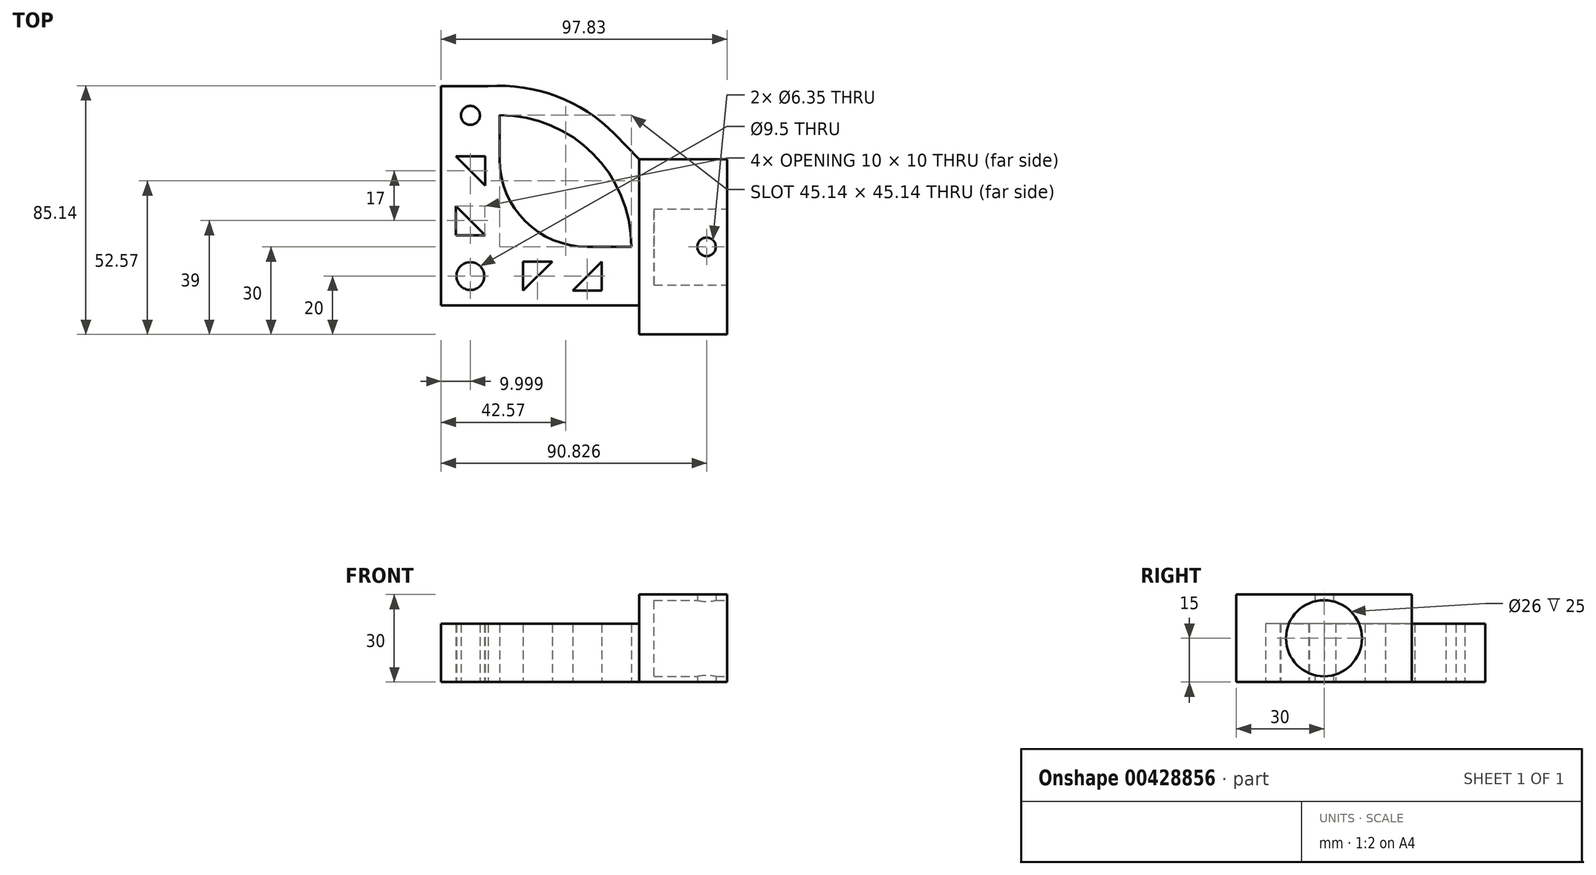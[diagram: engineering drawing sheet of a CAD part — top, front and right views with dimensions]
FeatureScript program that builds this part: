
annotation { "Feature Type Name" : "Feature", "Feature Type Description" : "" }
export const myFeature = defineFeature(function(context is Context, id is Id, definition is map)
    precondition{}
    {
        {
            var Q0;
            Q0=qCreatedBy(makeId("Top.planeOp"),FACE);
            var sketch = newSketch(context, id + "F0", { "sketchPlane" : qUnion([Q0])});
            skLineSegment(sketch, "E0.bottom", {"start": v(-29.45, 49.47) * mm, "end": v(-9.45, 49.47) * mm});
            skLineSegment(sketch, "E0.top", {"start": v(-29.45, -25.53) * mm, "end": v(-9.45, -25.53) * mm});
            skLineSegment(sketch, "E0.left", {"start": v(-29.45, 49.47) * mm, "end": v(-29.45, -25.53) * mm});
            skLineSegment(sketch, "E0.right", {"start": v(-9.45, 49.47) * mm, "end": v(-9.45, 24.47) * mm});
            skLineSegment(sketch, "E1.left", {"start": v(-9.45, -5.53) * mm, "end": v(-9.45, -25.53) * mm});
            skCircle(sketch, "E2", {"center": v(-19.45, -15.53) * mm, "radius": 4.75 * mm});
            skCircle(sketch, "E3", {"center": v(-19.45, 39.47) * mm, "radius": 3.25 * mm});
            skLineSegment(sketch, "E4", {"start": v(15.55, -20.53) * mm, "end": v(25.55, -10.53) * mm});
            skLineSegment(sketch, "E5", {"start": v(25.55, -10.53) * mm, "end": v(25.55, -20.53) * mm});
            skLineSegment(sketch, "E6", {"start": v(25.55, -20.53) * mm, "end": v(15.55, -20.53) * mm});
            skLineSegment(sketch, "E7", {"start": v(8.55, -10.53) * mm, "end": v(-1.45, -20.53) * mm});
            skLineSegment(sketch, "E8", {"start": v(-1.45, -20.53) * mm, "end": v(-1.45, -10.53) * mm});
            skLineSegment(sketch, "E9", {"start": v(-1.45, -10.53) * mm, "end": v(8.55, -10.53) * mm});
            skLineSegment(sketch, "E10", {"start": v(-14.45, 15.47) * mm, "end": v(-24.45, 25.47) * mm});
            skLineSegment(sketch, "E11", {"start": v(-24.45, 25.47) * mm, "end": v(-14.45, 25.47) * mm});
            skLineSegment(sketch, "E12", {"start": v(-14.45, 25.47) * mm, "end": v(-14.45, 15.47) * mm});
            skLineSegment(sketch, "E13", {"start": v(-24.45, 8.47) * mm, "end": v(-14.45, -1.53) * mm});
            skLineSegment(sketch, "E14", {"start": v(-14.45, -1.53) * mm, "end": v(-24.45, -1.53) * mm});
            skLineSegment(sketch, "E15", {"start": v(-24.45, -1.53) * mm, "end": v(-24.45, 8.47) * mm});
            skArc(sketch, "E16.filletArc", {"start": v(-9.45, 24.47) * mm, "mid": v(-0.66, 3.26) * mm, "end": v(20.55, -5.53) * mm});
            skLineSegment(sketch, "E17.bottom", {"start": v(38.38, -35.53) * mm, "end": v(68.38, -35.53) * mm});
            skLineSegment(sketch, "E17.top", {"start": v(38.38, 24.47) * mm, "end": v(68.38, 24.47) * mm});
            skLineSegment(sketch, "E17.right", {"start": v(68.38, -35.53) * mm, "end": v(68.38, 24.47) * mm});
            skLineSegment(sketch, "E18", {"start": v(-9.45, -25.53) * mm, "end": v(38.38, -25.53) * mm});
            skLineSegment(sketch, "E19", {"start": v(38.38, -5.53) * mm, "end": v(20.55, -5.53) * mm});
            skCircle(sketch, "E20", {"center": v(-9.45, -5.53) * mm, "radius": 55.14 * mm});
            skCircle(sketch, "E21", {"center": v(-9.45, -5.53) * mm, "radius": 45.14 * mm});
            skLineSegment(sketch, "E22", {"start": v(38.38, 24.47) * mm, "end": v(29.88, 33.12) * mm});
            skLineSegment(sketch, "E23", {"start": v(38.38, -5.53) * mm, "end": v(38.38, 24.47) * mm});
            skLineSegment(sketch, "E24", {"start": v(38.38, -25.53) * mm, "end": v(38.38, -35.53) * mm});
            skCircle(sketch, "E25", {"center": v(61.38, -5.53) * mm, "radius": 3.18 * mm});
            skLineSegment(sketch, "E26", {"start": v(38.38, -5.53) * mm, "end": v(38.38, -25.53) * mm});
            skSolve(sketch);
        }
        {
            var Q0;
            {var subQ5=sQuery(id+"F0.wireOp",EDGE,"E17.bottom");Q0=makeQuery(id+"F0.imprint","IMPRINT",FACE,{"disambiguationData":[TD([[makeQuery(id+"F0.imprint","IMPRINT",EDGE,{"derivedFrom":subQ5}),1.0]])]});}
            var Q1;
            {var subQ1=sQuery(id+"F0.wireOp",EDGE,"E18");var subQ5=sQuery(id+"F0.wireOp",EDGE,"E24");var subQ11=makeQuery(id+"F0.imprint","INTERSECT",VERTEX,{"derivedFrom":[subQ1,subQ5]});Q1=makeQuery(id+"F0.imprint","IMPRINT",FACE,{"disambiguationData":[TD([[makeQuery(id+"F0.imprint","IMPRINT",EDGE,{"disambiguationData":[TD([[subQ11,1.0]])],"derivedFrom":subQ1}),1.0]])]});}
            var Q2;
            {var subQ1=sQuery(id+"F0.wireOp",EDGE,"E0.top");Q2=makeQuery(id+"F0.imprint","IMPRINT",FACE,{"disambiguationData":[TD([[makeQuery(id+"F0.imprint","IMPRINT",EDGE,{"derivedFrom":subQ1}),1.0]])]});}
            var Q3;
            {var subQ8=sQuery(id+"F0.wireOp",EDGE,"E0.right");var subQ10=sQuery(id+"F0.wireOp",EDGE,"E0.bottom");var subQ11=makeQuery(id+"F0.imprint","INTERSECT",VERTEX,{"derivedFrom":[subQ10,subQ8]});Q3=makeQuery(id+"F0.imprint","IMPRINT",FACE,{"disambiguationData":[TD([[makeQuery(id+"F0.imprint","IMPRINT",EDGE,{"disambiguationData":[TD([[subQ11,1.0]])],"derivedFrom":subQ10}),-1.0]])]});}
            var Q4;
            {var subQ8=sQuery(id+"F0.wireOp",EDGE,"E0.right");var subQ9=sQuery(id+"F0.wireOp",EDGE,"E0.bottom");var subQ10=makeQuery(id+"F0.imprint","INTERSECT",VERTEX,{"derivedFrom":[subQ9,subQ8]});Q4=makeQuery(id+"F0.imprint","IMPRINT",FACE,{"disambiguationData":[TD([[makeQuery(id+"F0.imprint","IMPRINT",EDGE,{"disambiguationData":[TD([[subQ10,1.0]])],"derivedFrom":subQ9}),1.0]])]});}
            var Q5;
            {var subQ0=sQuery(id+"F0.wireOp",EDGE,"E0.left");var subQ1=sQuery(id+"F0.wireOp",EDGE,"E0.bottom");var subQ2=makeQuery(id+"F0.imprint","INTERSECT",VERTEX,{"derivedFrom":[subQ1,subQ0]});Q5=makeQuery(id+"F0.imprint","IMPRINT",FACE,{"disambiguationData":[TD([[makeQuery(id+"F0.imprint","IMPRINT",EDGE,{"disambiguationData":[TD([[subQ2,-1.0]])],"derivedFrom":subQ1}),-1.0]])]});}
            var Q6;
            {var subQ0=sQuery(id+"F0.wireOp",EDGE,"E22");Q6=makeQuery(id+"F0.imprint","IMPRINT",FACE,{"disambiguationData":[TD([[makeQuery(id+"F0.imprint","IMPRINT",EDGE,{"derivedFrom":subQ0}),1.0]])]});}
            extrude(context, id + "F1", {"entities" : qUnion([Q0, Q1, Q2, Q3, Q4, Q5, Q6]), "depth" : 20 * mm});
        }
        {
            var Q0;
            {var subQ5=sQuery(id+"F0.wireOp",EDGE,"E26");Q0=makeQuery(id+"F0.imprint","IMPRINT",FACE,{"disambiguationData":[TD([[makeQuery(id+"F0.imprint","IMPRINT",EDGE,{"derivedFrom":subQ5}),1.0]])]});}
            var Q1;
            {var subQ5=sQuery(id+"F0.wireOp",EDGE,"E17.bottom");Q1=makeQuery(id+"F0.imprint","IMPRINT",FACE,{"disambiguationData":[TD([[makeQuery(id+"F0.imprint","IMPRINT",EDGE,{"derivedFrom":subQ5}),1.0]])]});}
            extrude(context, id + "F2", {"entities" : qUnion([Q0, Q1]), "operationType" : NewBodyOperationType.ADD, "depth" : 30 * mm});
        }
        {
            var Q0;
            {var subQ0=sQuery(id+"F0.wireOp",EDGE,"E17.right");Q0=makeQuery(id+"F2.boolean.opBoolean","MERGE",FACE,{"derivedFrom":[makeQuery(id+"F1.opExtrude","SWEPT_FACE",FACE,{"disambiguationData":[OSD([subQ0])]}),makeQuery(id+"F2.opExtrude","SWEPT_FACE",FACE,{"disambiguationData":[OSD([subQ0])]})]});}
            var sketch = newSketch(context, id + "F3", { "sketchPlane" : qUnion([Q0])});
            skCircle(sketch, "E27", {"center": v(-5.53, 15) * mm, "radius": 13 * mm});
            skSolve(sketch);
        }
        {
            var Q0;
            Q0 = qSketchRegion(id + "F3", true);
            extrude(context, id + "F4", {"entities" : qUnion([Q0]), "operationType" : NewBodyOperationType.REMOVE, "oppositeDirection" : true, "depth" : 25 * mm});
        }
    });
